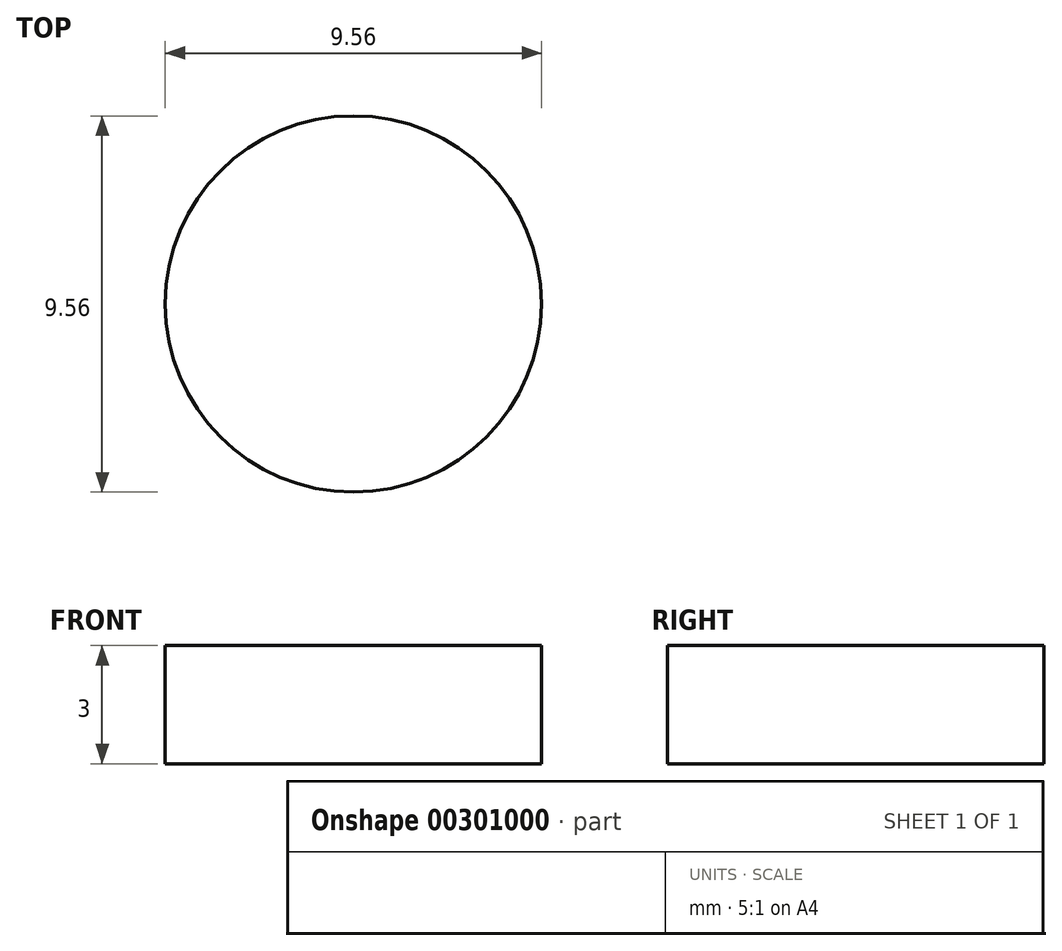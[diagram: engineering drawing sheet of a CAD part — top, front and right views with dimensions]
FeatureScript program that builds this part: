
annotation { "Feature Type Name" : "Feature", "Feature Type Description" : "" }
export const myFeature = defineFeature(function(context is Context, id is Id, definition is map)
    precondition{}
    {
        {
            var Q0;
            Q0=qCreatedBy(makeId("Top.planeOp"),FACE);
            var sketch = newSketch(context, id + "F0", { "sketchPlane" : qUnion([Q0])});
            skCircle(sketch, "E0", {"center": v(0, 0) * mm, "radius": 4.78 * mm});
            skSolve(sketch);
        }
        {
            var Q0;
            Q0=makeQuery(id+"F0.imprint","IMPRINT",FACE,{"disambiguationData":[TD([[makeQuery(id+"F0.imprint","IMPRINT",EDGE,{"derivedFrom":sQuery(id+"F0.wireOp",EDGE,"E0")}),1.0]])]});
            extrude(context, id + "F1", {"entities" : qUnion([Q0]), "depth" : 3 * mm, "offsetDistance" : 25 * mm});
        }
    });
